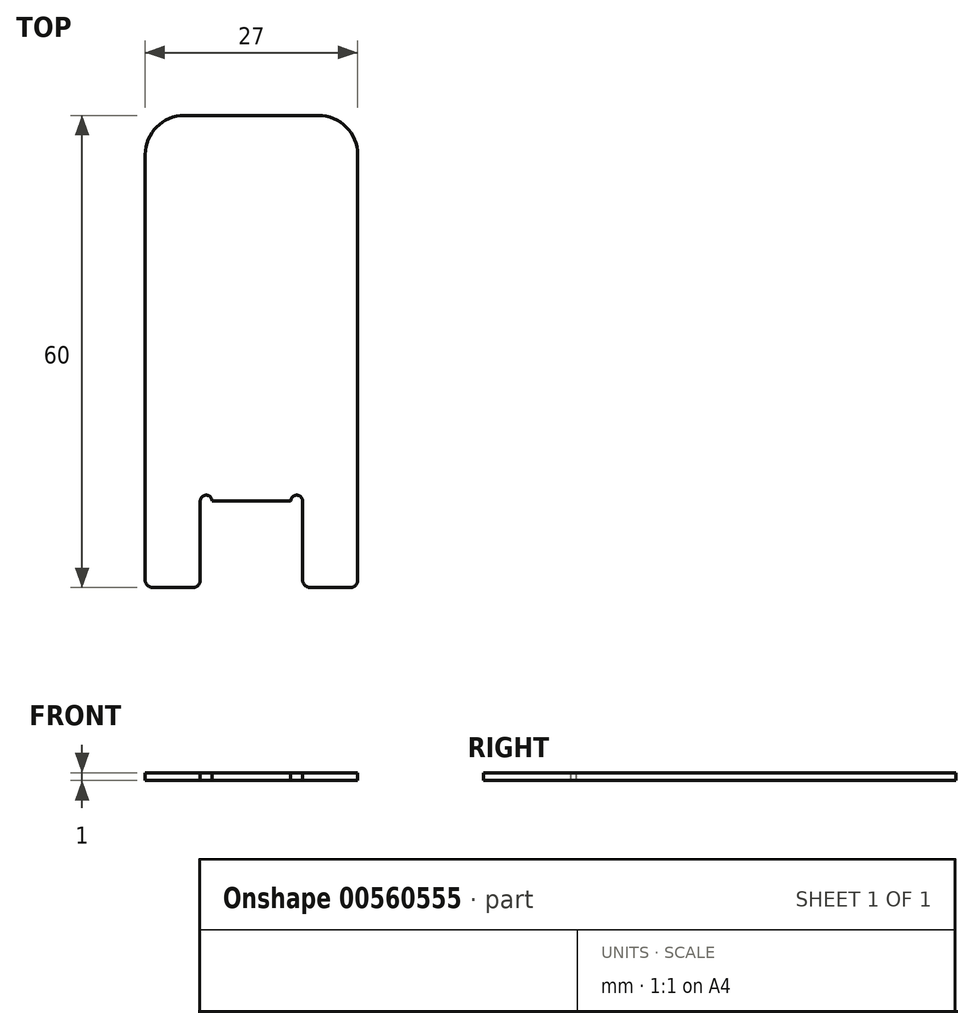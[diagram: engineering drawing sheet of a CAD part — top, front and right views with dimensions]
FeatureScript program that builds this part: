
annotation { "Feature Type Name" : "Feature", "Feature Type Description" : "" }
export const myFeature = defineFeature(function(context is Context, id is Id, definition is map)
    precondition{}
    {
        {
            var Q0;
            Q0=qCreatedBy(makeId("Top.planeOp"),FACE);
            var sketch = newSketch(context, id + "F0", { "sketchPlane" : qUnion([Q0])});
            skLineSegment(sketch, "E0.bottom", {"start": v(-12.5, 0) * mm, "end": v(-7.5, 0) * mm});
            skLineSegment(sketch, "E0.left", {"start": v(-13.5, 1) * mm, "end": v(-13.5, 55) * mm});
            skLineSegment(sketch, "E1", {"start": v(-6.5, 1) * mm, "end": v(-6.5, 11) * mm});
            skArc(sketch, "E2", {"start": v(-5, 11) * mm, "mid": v(-5.75, 11.75) * mm, "end": v(-6.5, 11) * mm});
            skLineSegment(sketch, "E3", {"start": v(-8.5, 60) * mm, "end": v(0, 60) * mm});
            skLineSegment(sketch, "E4.trimOffspring", {"start": v(-5, 11) * mm, "end": v(0, 11) * mm});
            skLineSegment(sketch, "E5", {"start": v(0, 70.54) * mm, "end": v(0, -4.63) * mm, "construction": true});
            skPoint(sketch, "E6.visualSharp", {"position": v(-6.5, 0) * mm});
            skArc(sketch, "E6.filletArc", {"start": v(-7.5, 0) * mm, "mid": v(-6.8, 0.3) * mm, "end": v(-6.5, 1) * mm});
            skPoint(sketch, "E7.visualSharp", {"position": v(-13.5, 0) * mm});
            skArc(sketch, "E7.filletArc", {"start": v(-13.5, 1) * mm, "mid": v(-13.2, 0.3) * mm, "end": v(-12.5, 0) * mm});
            skPoint(sketch, "E8.visualSharp", {"position": v(-13.5, 60) * mm});
            skArc(sketch, "E8.filletArc", {"start": v(-8.5, 60) * mm, "mid": v(-12.04, 58.54) * mm, "end": v(-13.5, 55) * mm});
            skArc(sketch, "E9.MirrorCS", {"start": v(5, 11) * mm, "mid": v(5.75, 11.75) * mm, "end": v(6.5, 11) * mm});
            skArc(sketch, "E10.MirrorCS", {"start": v(7.5, 0) * mm, "mid": v(6.8, 0.3) * mm, "end": v(6.5, 1) * mm});
            skArc(sketch, "E11.MirrorCS", {"start": v(13.5, 1) * mm, "mid": v(13.2, 0.3) * mm, "end": v(12.5, 0) * mm});
            skArc(sketch, "E12.MirrorCS", {"start": v(8.5, 60) * mm, "mid": v(12.04, 58.54) * mm, "end": v(13.5, 55) * mm});
            skLineSegment(sketch, "E13.MirrorCS", {"start": v(13.5, 1) * mm, "end": v(13.5, 55) * mm});
            skLineSegment(sketch, "E14.MirrorCS", {"start": v(8.5, 60) * mm, "end": v(0, 60) * mm});
            skPoint(sketch, "E15.MirrorP", {"position": v(13.5, 0) * mm});
            skPoint(sketch, "E16.MirrorP", {"position": v(6.5, 0) * mm});
            skLineSegment(sketch, "E17.MirrorCS", {"start": v(12.5, 0) * mm, "end": v(7.5, 0) * mm});
            skLineSegment(sketch, "E18.MirrorCS", {"start": v(6.5, 1) * mm, "end": v(6.5, 11) * mm});
            skLineSegment(sketch, "E19.MirrorCS", {"start": v(5, 11) * mm, "end": v(0, 11) * mm});
            skPoint(sketch, "E20.MirrorP", {"position": v(13.5, 60) * mm});
            skSolve(sketch);
        }
        {
            var Q0;
            Q0=makeQuery(id+"F0.imprint","IMPRINT",FACE,{"disambiguationData":[TD([[makeQuery(id+"F0.imprint","IMPRINT",EDGE,{"derivedFrom":sQuery(id+"F0.wireOp",EDGE,"E0.bottom")}),1.0]])]});
            extrude(context, id + "F1", {"entities" : qUnion([Q0]), "depth" : 1 * mm, "offsetDistance" : 25 * mm});
        }
    });
